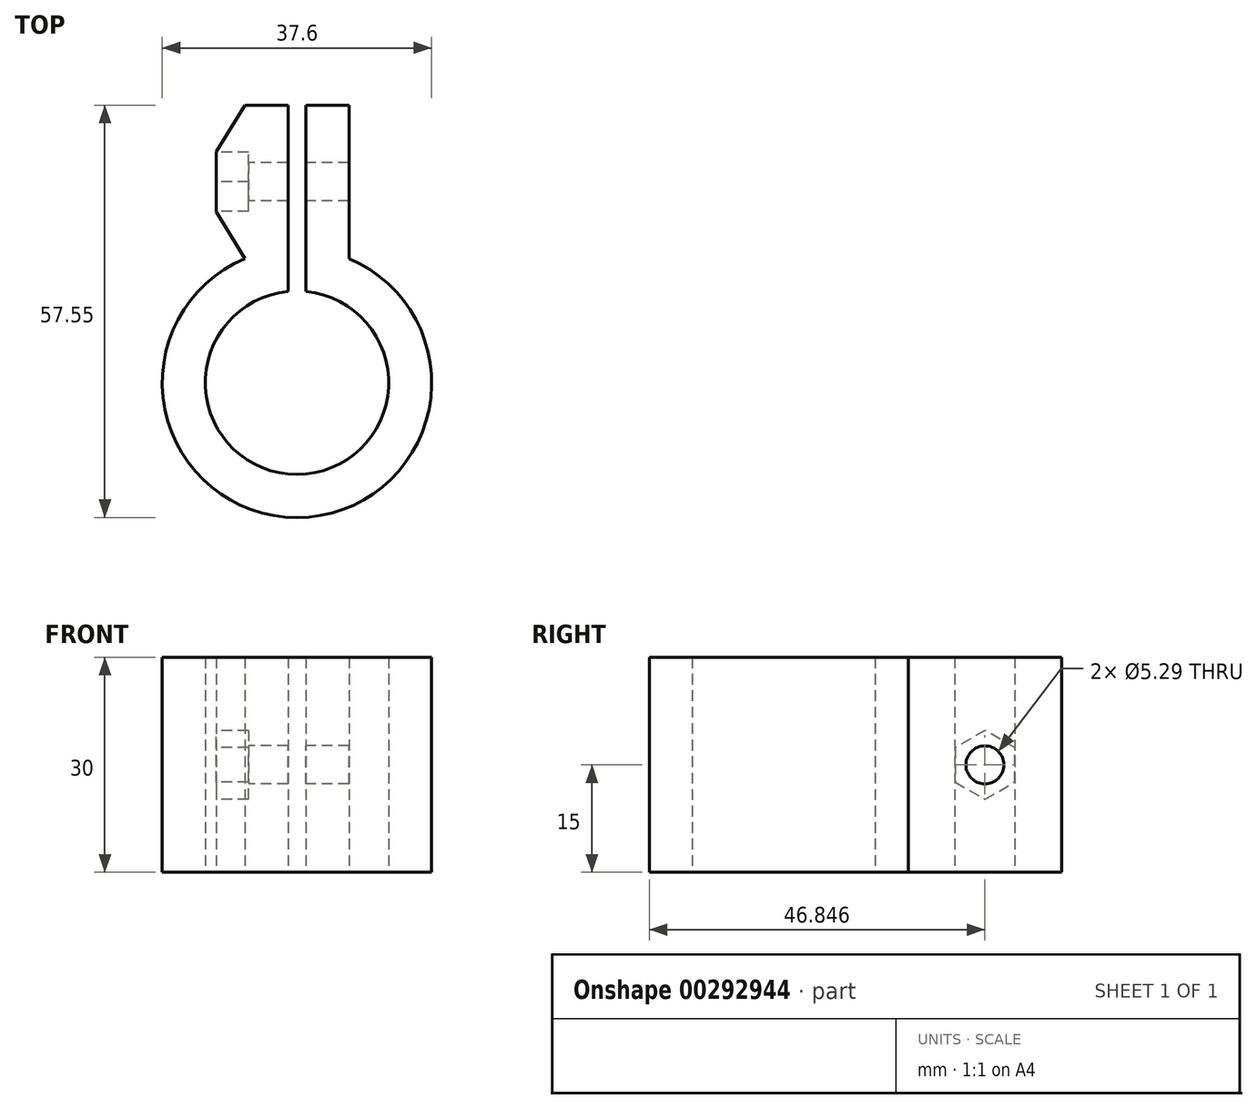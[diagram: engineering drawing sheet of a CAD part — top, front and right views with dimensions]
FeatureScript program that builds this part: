
annotation { "Feature Type Name" : "Feature", "Feature Type Description" : "" }
export const myFeature = defineFeature(function(context is Context, id is Id, definition is map)
    precondition{}
    {
        {
            var Q0;
            Q0=qCreatedBy(makeId("Top.planeOp"),FACE);
            var sketch = newSketch(context, id + "F0", { "sketchPlane" : qUnion([Q0])});
            skArc(sketch, "E0", {"start": v(-1.25, 12.74) * mm, "mid": v(0, -12.8) * mm, "end": v(1.25, 12.74) * mm});
            skArc(sketch, "E1", {"start": v(-7.25, 17.35) * mm, "mid": v(0, -18.8) * mm, "end": v(7.25, 17.35) * mm});
            skLineSegment(sketch, "E2", {"start": v(-1.25, 38.75) * mm, "end": v(-7.25, 38.75) * mm});
            skLineSegment(sketch, "E3", {"start": v(-7.25, 38.75) * mm, "end": v(-7.25, 17.35) * mm});
            skLineSegment(sketch, "E4", {"start": v(1.25, 38.74) * mm, "end": v(7.25, 38.74) * mm});
            skLineSegment(sketch, "E5", {"start": v(7.25, 38.74) * mm, "end": v(7.25, 17.35) * mm});
            skLineSegment(sketch, "E6", {"start": v(-1.25, 38.75) * mm, "end": v(-1.25, 12.74) * mm});
            skLineSegment(sketch, "E7", {"start": v(1.25, 38.74) * mm, "end": v(1.25, 12.74) * mm});
            skPoint(sketch, "E8.0.midPoint", {"position": v(-7.25, 38.75) * mm});
            skLineSegment(sketch, "E9.left", {"start": v(-11.25, 32.25) * mm, "end": v(-11.25, 23.85) * mm});
            skLineSegment(sketch, "E10", {"start": v(-7.25, 38.75) * mm, "end": v(-11.25, 32.25) * mm});
            skLineSegment(sketch, "E11", {"start": v(-11.25, 23.85) * mm, "end": v(-7.25, 17.35) * mm});
            skSolve(sketch);
        }
        {
            var Q0;
            Q0 = qSketchRegion(id + "F0", true);
            extrude(context, id + "F1", {"entities" : qUnion([Q0]), "depth" : 30 * mm});
        }
        {
            var Q0;
            Q0=makeQuery(id+"F1.opExtrude","SWEPT_FACE",FACE,{"disambiguationData":[OSD([sQuery(id+"F0.wireOp",EDGE,"E9.left")])]});
            var sketch = newSketch(context, id + "F2", { "sketchPlane" : qUnion([Q0])});
            skCircle(sketch, "E12.cCircle", {"center": v(-28.05, 15) * mm, "radius": 4.15 * mm, "construction": true});
            skPoint(sketch, "E12.cCircle.centerSnap0", {"position": v(-28.05, 30) * mm});
            skPoint(sketch, "E12.cCircle.centerSnap1", {"position": v(-23.9, 15) * mm});
            skLineSegment(sketch, "E12.0", {"start": v(-32.2, 12.6) * mm, "end": v(-32.2, 17.4) * mm});
            skLineSegment(sketch, "E12.1", {"start": v(-32.2, 17.4) * mm, "end": v(-28.05, 19.8) * mm});
            skLineSegment(sketch, "E12.2", {"start": v(-28.05, 19.8) * mm, "end": v(-23.9, 17.4) * mm});
            skLineSegment(sketch, "E12.3", {"start": v(-23.9, 17.4) * mm, "end": v(-23.9, 12.6) * mm});
            skLineSegment(sketch, "E12.4", {"start": v(-23.9, 12.6) * mm, "end": v(-28.05, 10.2) * mm});
            skLineSegment(sketch, "E12.5", {"start": v(-28.05, 10.2) * mm, "end": v(-32.2, 12.6) * mm});
            skPoint(sketch, "E12.0.midPoint", {"position": v(-32.2, 15) * mm});
            skSolve(sketch);
        }
        {
            var Q0;
            Q0=makeQuery(id+"F2.imprint","IMPRINT",FACE,{"disambiguationData":[TD([[makeQuery(id+"F2.imprint","IMPRINT",EDGE,{"derivedFrom":sQuery(id+"F2.wireOp",EDGE,"E12.0")}),-1.0]])]});
            extrude(context, id + "F3", {"entities" : qUnion([Q0]), "operationType" : NewBodyOperationType.REMOVE, "oppositeDirection" : true, "depth" : 4.5 * mm});
        }
        {
            var Q0;
            Q0=makeQuery(id+"F3.boolean.opBoolean","COPY",FACE,{"derivedFrom":makeQuery(id+"F3.opExtrude","CAP_FACE",FACE,{"disambiguationData":[OSD([sQuery(id+"F2.wireOp",EDGE,"E12.0"),sQuery(id+"F2.wireOp",EDGE,"E12.1"),sQuery(id+"F2.wireOp",EDGE,"E12.2"),sQuery(id+"F2.wireOp",EDGE,"E12.3"),sQuery(id+"F2.wireOp",EDGE,"E12.4"),sQuery(id+"F2.wireOp",EDGE,"E12.5")])],"isStart":false})});
            var sketch = newSketch(context, id + "F4", { "sketchPlane" : qUnion([Q0])});
            skCircle(sketch, "E13", {"center": v(-28.05, 15) * mm, "radius": 2.65 * mm});
            skPoint(sketch, "E13.centerSnap0", {"position": v(-23.9, 15) * mm});
            skSolve(sketch);
        }
        {
            var Q0;
            Q0=makeQuery(id+"F4.imprint","IMPRINT",FACE,{"disambiguationData":[TD([[makeQuery(id+"F4.imprint","IMPRINT",EDGE,{"derivedFrom":sQuery(id+"F4.wireOp",EDGE,"E13")}),1.0]])]});
            extrude(context, id + "F5", {"entities" : qUnion([Q0]), "operationType" : NewBodyOperationType.REMOVE, "endBound" : BoundingType.THROUGH_ALL, "oppositeDirection" : true, "depth" : 25 * mm});
        }
    });
